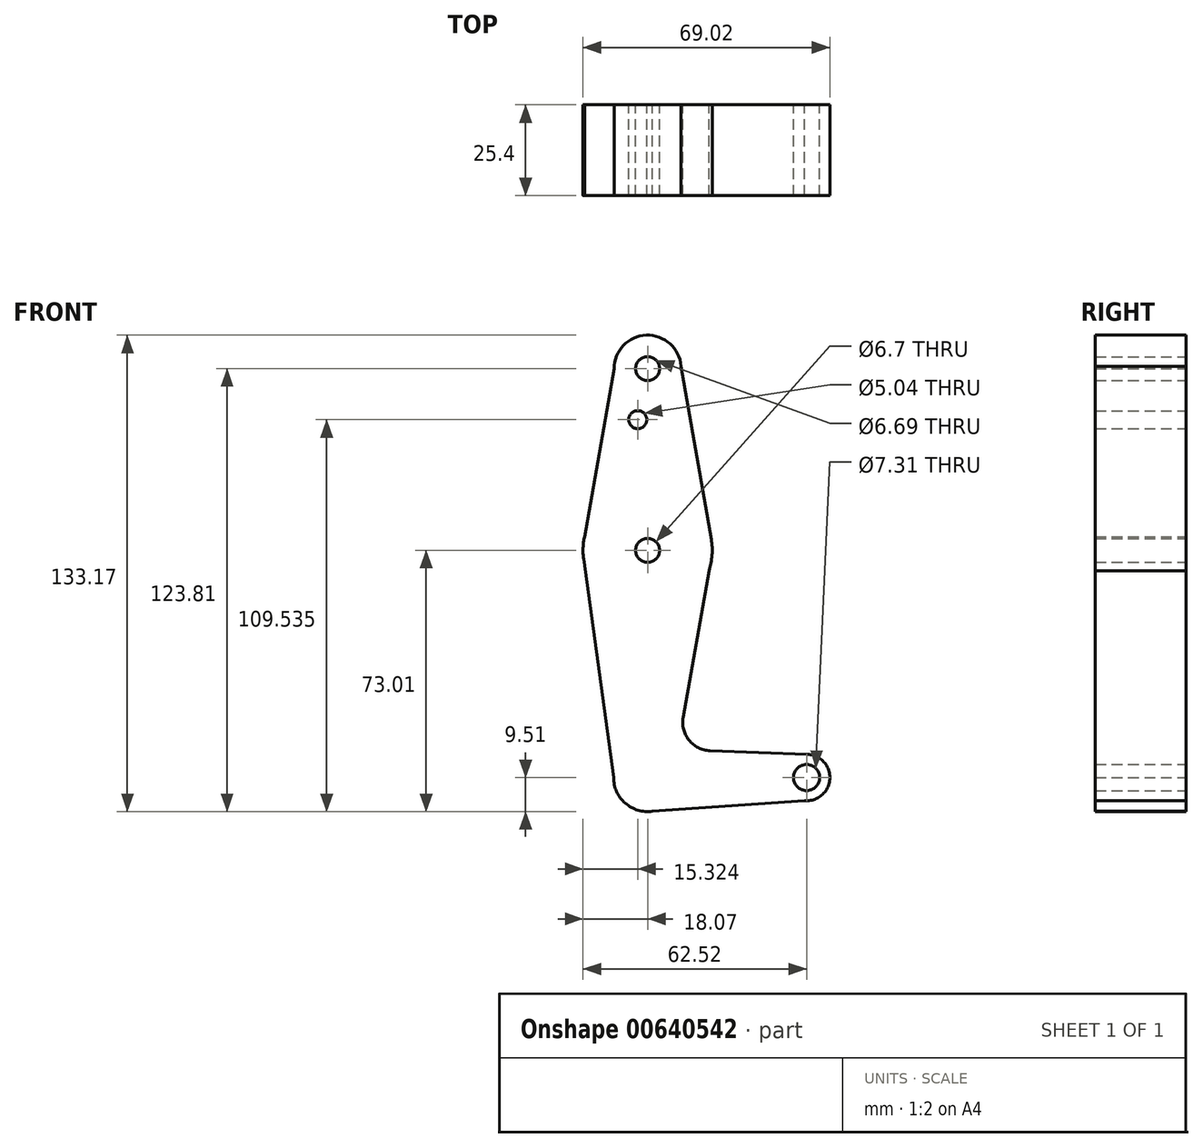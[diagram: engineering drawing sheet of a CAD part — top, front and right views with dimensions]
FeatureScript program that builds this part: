
annotation { "Feature Type Name" : "Feature", "Feature Type Description" : "" }
export const myFeature = defineFeature(function(context is Context, id is Id, definition is map)
    precondition{}
    {
        {
            var Q0;
            Q0=qCreatedBy(makeId("Front.planeOp"),FACE);
            var sketch = newSketch(context, id + "F0", { "sketchPlane" : qUnion([Q0])});
            skLineSegment(sketch, "E0", {"start": v(0, 0) * mm, "end": v(44.45, 0) * mm, "construction": true});
            skCircle(sketch, "E1", {"center": v(0, 114.3) * mm, "radius": 9.36 * mm});
            skCircle(sketch, "E2", {"center": v(0, 0) * mm, "radius": 9.5 * mm});
            skCircle(sketch, "E3", {"center": v(44.45, 0) * mm, "radius": 6.5 * mm});
            skCircle(sketch, "E4", {"center": v(0, 63.5) * mm, "radius": 18.07 * mm});
            skLineSegment(sketch, "E5", {"start": v(-17.9, 65.96) * mm, "end": v(-9.36, 114.3) * mm});
            skLineSegment(sketch, "E6", {"start": v(-9.5, 0) * mm, "end": v(-17.9, 61.04) * mm});
            skLineSegment(sketch, "E7", {"start": v(9.34, 114.99) * mm, "end": v(17.8, 66.61) * mm});
            skLineSegment(sketch, "E8", {"start": v(18.06, 62.94) * mm, "end": v(9.92, 16.83) * mm});
            skLineSegment(sketch, "E9", {"start": v(17.45, 7.5) * mm, "end": v(44.7, 6.5) * mm});
            skLineSegment(sketch, "E10", {"start": v(0, -9.5) * mm, "end": v(45.98, -6.32) * mm});
            skCircle(sketch, "E11", {"center": v(-2.75, 100.03) * mm, "radius": 2.52 * mm});
            skCircle(sketch, "E12", {"center": v(0, 114.3) * mm, "radius": 3.35 * mm});
            skCircle(sketch, "E13", {"center": v(0, 63.5) * mm, "radius": 3.35 * mm});
            skCircle(sketch, "E14", {"center": v(44.45, 0) * mm, "radius": 3.65 * mm});
            skPoint(sketch, "E15.visualSharp", {"position": v(8.33, 7.84) * mm});
            skArc(sketch, "E15.filletArc", {"start": v(9.92, 16.83) * mm, "mid": v(11.56, 10.45) * mm, "end": v(17.45, 7.5) * mm});
            skLineSegment(sketch, "E16", {"start": v(0, 0) * mm, "end": v(0, 114.3) * mm, "construction": true});
            skSolve(sketch);
        }
        {
            var Q0;
            Q0 = qSketchRegion(id + "F0", true);
            extrude(context, id + "F1", {"entities" : qUnion([Q0]), "depth" : 25.4 * mm, "offsetDistance" : 25.4 * mm});
        }
    });
